# Revit family: URA_Eclairage_de_Securite_URAONE
name_source: partatom
category: Luminaires
units: mm (PartAtom-declared; Revit-internal decimal feet)

## family parameters
Cote de connecteur circulaire = Utiliser le diamètre
Couper avec des vides une fois chargée = Non
Hôte = Face
Partagée = Non
Point de calcul de pièce = Non
Source d'éclairage = Oui
Type d'élément = Normal

## types (18) — shared parameters
Angle de l'inclinaison = 60.00°
CLASSE_DE_PROTECTION = II
CLASSE_DE_PROTECTION_(IP) = IP42
COULEUR_DU_BOITIER = blanc
Condition Générale d'Utilisation = https://export.legrand.com
DUREE_DE_GARANTIE_BAES_COMPLET = 2
Elévation par défaut = 1219 mm
FORMAT_PRODUIT = rectangle
Fichier de distribution photométrique = generic
Filtre de couleur = 16777215
Gradation des changements de température de couleur de lampe = <Aucun>
INSTALLATION_DE_SURVEILLANCE = auto-test automatique
MATERIAU_DU_BOITIER = plastique

## per-type parameters (varying)
| type | ADAPTE_AU_TYPE_DE_MARQUAGE | ALIMENTATION | CATEGORIE_PRODUIT | DISTANCE_DE_RECONNAISSANCE | ETAT_DES_ACCUS | FLUX_LUMINEUX_EN_MODE_D'URGENCE | FONCTION | HAUTEUR/PROFONDEUR | LARGEUR | LONGUEUR | MATERIAU_DU_COUVERCLE | PUISSANCE_DE_LA_LAMPE | REFERENCE_ARTICLE | REF_BATTERIE_DE_RECHANGE | RESERVE_DE_MARCHE | SOURCE_LUMINEUSE | TENSION_NOMINALE_(MAX) | TENSION_NOMINALE_(MIN) | TYPE_DE_COMMUTATION | TYPE_DE_MONTAGE | TYPE_DE_TENSION |
| BAES URAONE EVAC SATI LEDS | feuillet/plaque inséré(e) | décentralisé (batterie individuelle) | Autonome | 15 | NiCd | 45 | Evac | 41 | 110 | 210 | plastique transparent | 0.5 | 111013 | 111906 | 1 | LED non interchangeable | 253 | 207 | mode veille | pose murale en saillie | CA |
| BAES URAONE AMBIANCE SATI LEDS |  | décentralisé (batterie individuelle) | Autonome | 15 | NiMh | 320 | Amb | 41 | 110 | 210 | plastique transparent | 4 | 111227 | 111907 | 1 | LED non interchangeable | 253 | 207 | mode veille | pose murale en saillie | CA |
| BAES + BAEH URAONE SATI | feuillet/plaque inséré(e) | décentralisé (batterie individuelle) | Autonome | 15 | NiCd | 45 | BAES+BAEH | 41 | 110 | 210 | plastique transparent | 0.72 | 111248 | 2*111906 | 1 | LED non interchangeable | 253 | 207 | mode veille | pose murale en saillie | CA |
| BAES + DBR URAONE SATI | feuillet/plaque inséré(e) | décentralisé (batterie individuelle) | Autonome | 15 | NiCd | 45 | DBR | 41 | 110 | 210 | plastique transparent | 1 | 111257 | 111901 | 1 | LED non interchangeable | 253 | 207 | mode veille | pose murale en saillie | CA |
| BAES URALIGHT AMB ADR |  | décentralisé (batterie individuelle) | Autonome | 15 | NiCd | 360 | Amb | 74.75 | 147.8 | 336 | plastique transparent | 8 | 112002 | 186003 | 1 | lampe fluorescente | 253 | 207 | mode veille | pose murale en saillie | CA |
| BAES URAONE EVAC ADR LEDS | feuillet/plaque inséré(e) | décentralisé (batterie individuelle) | Autonome | 15 | NiCd | 45 | Evac | 41 | 110 | 210 | plastique transparent | 0.5 | 112013 | 111906 | 1 | LED non interchangeable | 253 | 207 | mode veille | pose murale en saillie | CA |
| BAES URAONE AMBIANCE ADR LEDS |  | décentralisé (batterie individuelle) | Autonome | 15 | NiMh | 230 | Amb | 41 | 110 | 210 | plastique transparent | 4 | 112229 | 111907 | 1 | LED non interchangeable | 253 | 207 | mode veille | pose murale en saillie | CA |
| BAES + BAEH URAONE ADR | feuillet/plaque inséré(e) | décentralisé (batterie individuelle) | Autonome | 15 | NiCd | 45 | BAES+BAEH | 41 | 110 | 210 | plastique transparent | 0.72 | 112249 | 2*111906 | 1 | LED non interchangeable | 253 | 207 | mode veille | pose murale en saillie | CA |
| BAES + DBR URAONE ADR | feuillet/plaque inséré(e) | décentralisé (batterie individuelle) | Autonome | 15 | NiCd | 45 | DBR | 41 | 110 | 210 | plastique transparent | 1 | 112259 | 111901 | 1 | LED non interchangeable | 253 | 207 | mode veille | pose murale en saillie | CA |
| BAEH URAONE SATI LEDS | feuillet/plaque inséré(e) | décentralisé (batterie individuelle) | Autonome | 15 | NiCd | 8 | BAEH | 41 | 110 | 210 | plastique transparent | 0.09 | 113013 | 111906 | 5 | LED non interchangeable | 253 | 207 | mode veille | pose murale en saillie | CA |
| BAEH URAONE ADR LEDS | feuillet/plaque inséré(e) | décentralisé (batterie individuelle) | Autonome | 15 | NiCd | 8 | BAEH | 41 | 110 | 210 | plastique transparent | 0.09 | 113023 | 111906 | 5 | LED non interchangeable | 253 | 207 | mode veille | pose murale en saillie | CA |
| BAES URAONE EVAC AUTODIAG LEDS | feuillet/plaque inséré(e) | décentralisé (batterie individuelle) | Autonome | 15 | NiCd | 45 | Evac | 41 | 110 | 210 | plastique transparent | 0.5 | 113218 | 111906 | 1 | LED non interchangeable | 253 | 207 | mode veille | pose murale en saillie | CA |
| BAES URAONE AMB AUTODIAG LEDS |  | décentralisé (batterie individuelle) | Autonome | 15 | NiMh | 320 | Amb | 41 | 110 | 210 | plastique transparent | 4 | 113228 | 111907 | 1 | LED non interchangeable | 253 | 207 | mode veille | pose murale en saillie | CA |
| BAEH URAONE AUTODIAG LEDS | feuillet/plaque inséré(e) | décentralisé (batterie individuelle) | Autonome | 15 | NiCd | 8 | BAEH | 41 | 110 | 210 | plastique transparent | 0.09 | 113238 | 111906 | 5 | LED non interchangeable | 253 | 207 | mode veille | pose murale en saillie | CA |
| BAES + BAEH URAONE AUTODIAG | feuillet/plaque inséré(e) | décentralisé (batterie individuelle) | Autonome | 15 | NiCd | 45 | BAES+BAEH | 41 | 110 | 210 | plastique transparent | 0.72 | 113248 | 2*111906 | 1 | LED non interchangeable | 253 | 207 | mode veille | pose murale en saillie | CA |
| URAONE DBR (BAES+DBR) AUTODIAG tout LEDs |  | central (batterie centrale) | Autonome |  | NiCd | 45 | DBR | 41 | 110 | 210 | verre transparent | 12 | 113258 | 111901 | 1 | LED non interchangeable | 253 | 207 | circuit permanent/circuit de secours | montage en saillie/encastrement | CA |
| LSC URAONE AMBIANCE 110/230 |  | central (batterie centrale) | LSC | 15 | non applicable | 320 | Amb | 41 | 110 | 210 | plastique transparent | 4 | 122224 |  |  | LED non interchangeable | 230 | 110 | circuit permanent/circuit de secours | montage en saillie/encastrement | CA/CC |
| LSC URAONE AMBIANCE 24/48 |  | central (batterie centrale) | LSC | 15 | non applicable | 320 | Amb | 41 | 110 | 210 | plastique transparent | 4 | 122225 |  |  | LED non interchangeable | 48 | 24 | circuit permanent/circuit de secours | montage en saillie/encastrement | CC |

note: column(s) folded — value = type name in every type: DESIGNATION_ARTICLE

## geometry (parser evidence)
native form markers: Blend x10
no freeform markers — native parametric forms only
